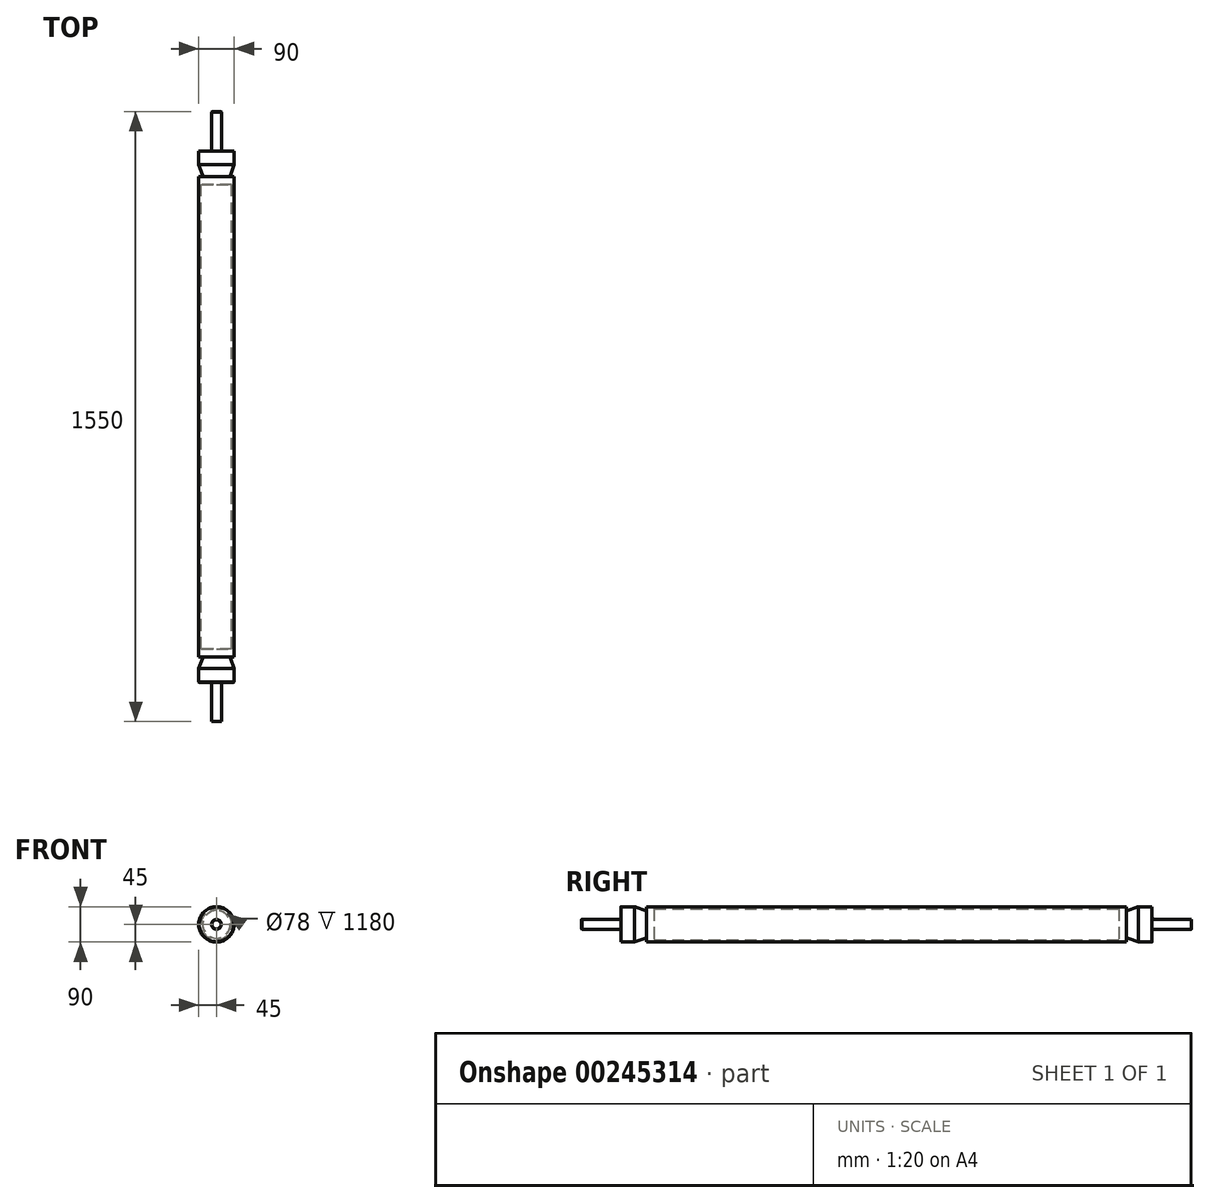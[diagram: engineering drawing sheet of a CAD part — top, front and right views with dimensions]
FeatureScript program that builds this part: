
annotation { "Feature Type Name" : "Feature", "Feature Type Description" : "" }
export const myFeature = defineFeature(function(context is Context, id is Id, definition is map)
    precondition{}
    {
        {
            var Q0;
            Q0=qCreatedBy(makeId("Right.planeOp"),FACE);
            var sketch = newSketch(context, id + "F0", { "sketchPlane" : qUnion([Q0])});
            skLineSegment(sketch, "E0", {"start": v(0, 0) * mm, "end": v(0, 12.5) * mm});
            skLineSegment(sketch, "E1", {"start": v(0, 12.5) * mm, "end": v(100, 12.5) * mm});
            skLineSegment(sketch, "E2", {"start": v(100, 12.5) * mm, "end": v(100, 45) * mm});
            skLineSegment(sketch, "E3", {"start": v(165, 45) * mm, "end": v(165, 38.37) * mm});
            skLineSegment(sketch, "E4", {"start": v(165, 45) * mm, "end": v(1385, 45) * mm});
            skLineSegment(sketch, "E5", {"start": v(1385, 38.37) * mm, "end": v(1385, 45) * mm});
            skLineSegment(sketch, "E6", {"start": v(1415, 45) * mm, "end": v(1450, 45) * mm});
            skLineSegment(sketch, "E7", {"start": v(1450, 45) * mm, "end": v(1450, 12.5) * mm});
            skLineSegment(sketch, "E8", {"start": v(1450, 12.5) * mm, "end": v(1550, 12.5) * mm});
            skLineSegment(sketch, "E9", {"start": v(1550, 12.5) * mm, "end": v(1550, 0) * mm});
            skLineSegment(sketch, "E10", {"start": v(1550, 0) * mm, "end": v(1365, 0) * mm});
            skLineSegment(sketch, "E11", {"start": v(160.97, 35.55) * mm, "end": v(135, 45) * mm});
            skLineSegment(sketch, "E12", {"start": v(1389.03, 35.55) * mm, "end": v(1415, 45) * mm});
            skLineSegment(sketch, "E13", {"start": v(135, 45) * mm, "end": v(100, 45) * mm});
            skPoint(sketch, "E14.visualSharp", {"position": v(165, 34.08) * mm});
            skArc(sketch, "E14.filletArc", {"start": v(160.97, 35.55) * mm, "mid": v(163.72, 35.9) * mm, "end": v(165, 38.37) * mm});
            skPoint(sketch, "E15.visualSharp", {"position": v(1385, 34.08) * mm});
            skArc(sketch, "E15.filletArc", {"start": v(1385, 38.37) * mm, "mid": v(1386.28, 35.9) * mm, "end": v(1389.03, 35.55) * mm});
            skLineSegment(sketch, "E16", {"start": v(185, 39) * mm, "end": v(1365, 39) * mm});
            skLineSegment(sketch, "E17", {"start": v(1365, 39) * mm, "end": v(1365, 0) * mm});
            skLineSegment(sketch, "E18", {"start": v(185, 39) * mm, "end": v(185, 0) * mm});
            skLineSegment(sketch, "E19.trimOffspring", {"start": v(185, 0) * mm, "end": v(0, 0) * mm});
            skSolve(sketch);
        }
        {
            var Q0;
            Q0=makeQuery(id+"F0.imprint","IMPRINT",FACE,{"disambiguationData":[TD([[makeQuery(id+"F0.imprint","IMPRINT",EDGE,{"derivedFrom":sQuery(id+"F0.wireOp",EDGE,"E0")}),-1.0]])]});
            var Q1;
            Q1=sQuery(id+"F0.wireOp",EDGE,"E10");
            revolve(context, id + "F1", {"surfaceOperationType" : NewSurfaceOperationType.NEW, "entities" : qUnion([Q0]), "axis" : qUnion([Q1]), "revolveType" : RevolveType.FULL});
        }
        {
            var Q0;
            Q0=makeQuery(id+"F1.opRevolve","SWEPT_EDGE",EDGE,{"disambiguationData":[OSD([sQuery(id+"F0.wireOp",EDGE,"E7"),sQuery(id+"F0.wireOp",EDGE,"E8")])]});
            var Q1;
            Q1=makeQuery(id+"F1.opRevolve","SWEPT_EDGE",EDGE,{"disambiguationData":[OSD([sQuery(id+"F0.wireOp",EDGE,"E1"),sQuery(id+"F0.wireOp",EDGE,"E2")])]});
            fillet(context, id + "F2", {"entities" : qUnion([Q0, Q1]), "tangentPropagation" : true, "radius" : 5 * mm, "defaultsChanged" : false, "vertexSettings" : [], "allowEdgeOverflow" : false});
        }
        {
            var Q0;
            Q0=makeQuery(id+"F1.opRevolve","SWEPT_EDGE",EDGE,{"disambiguationData":[OSD([sQuery(id+"F0.wireOp",EDGE,"E6"),sQuery(id+"F0.wireOp",EDGE,"E7")])]});
            var Q1;
            Q1=makeQuery(id+"F1.opRevolve","SWEPT_EDGE",EDGE,{"disambiguationData":[OSD([sQuery(id+"F0.wireOp",EDGE,"E8"),sQuery(id+"F0.wireOp",EDGE,"E9")])]});
            var Q2;
            Q2=makeQuery(id+"F1.opRevolve","SWEPT_EDGE",EDGE,{"disambiguationData":[OSD([sQuery(id+"F0.wireOp",EDGE,"E0"),sQuery(id+"F0.wireOp",EDGE,"E1")])]});
            var Q3;
            Q3=makeQuery(id+"F1.opRevolve","SWEPT_EDGE",EDGE,{"disambiguationData":[OSD([sQuery(id+"F0.wireOp",EDGE,"E2"),sQuery(id+"F0.wireOp",EDGE,"E13")])]});
            chamfer(context, id + "F3", {"entities" : qUnion([Q0, Q1, Q2, Q3]), "width" : 1 * mm, "tangentPropagation" : true});
        }
    });
